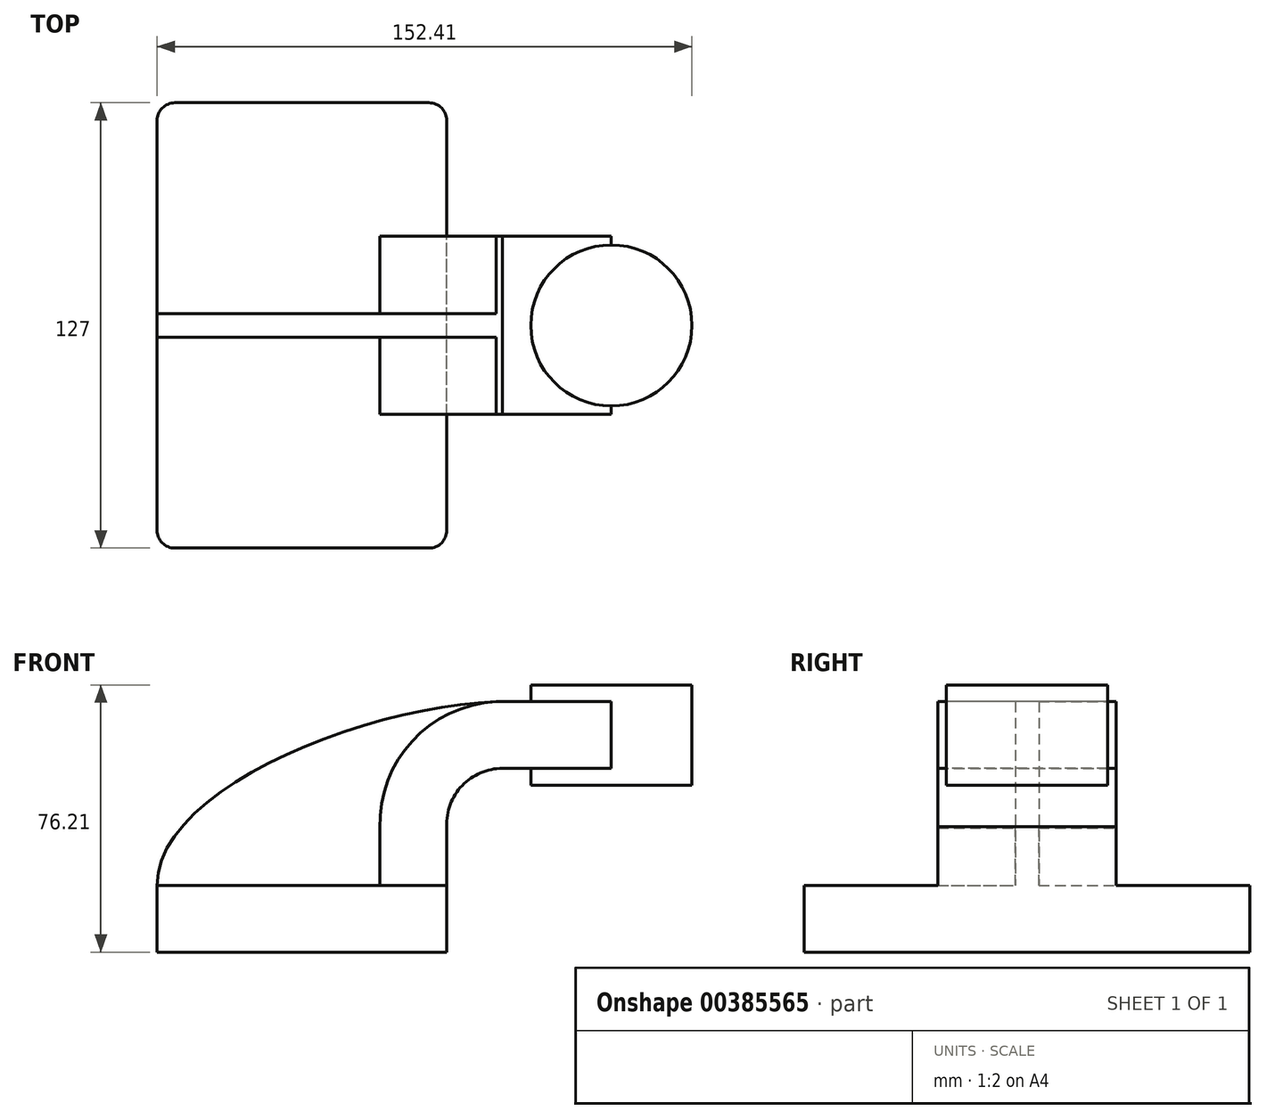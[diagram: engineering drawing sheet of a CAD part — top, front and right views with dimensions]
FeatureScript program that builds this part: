
annotation { "Feature Type Name" : "Feature", "Feature Type Description" : "" }
export const myFeature = defineFeature(function(context is Context, id is Id, definition is map)
    precondition{}
    {
        {
            var Q0;
            Q0=qCreatedBy(makeId("Front.planeOp"),FACE);
            var sketch = newSketch(context, id + "F0", { "sketchPlane" : qUnion([Q0])});
            skLineSegment(sketch, "E0.bottom", {"start": v(-41.28, 9.53) * mm, "end": v(41.27, 9.53) * mm});
            skLineSegment(sketch, "E0.top", {"start": v(-41.28, -9.52) * mm, "end": v(41.28, -9.52) * mm});
            skLineSegment(sketch, "E0.left", {"start": v(-41.28, 9.53) * mm, "end": v(-41.27, -9.52) * mm});
            skLineSegment(sketch, "E0.right", {"start": v(41.28, 9.53) * mm, "end": v(41.28, -9.52) * mm});
            skPoint(sketch, "E0.middle", {"position": v(0, 0) * mm});
            skLineSegment(sketch, "E1.bottom", {"start": v(60.33, 66.68) * mm, "end": v(111.12, 66.68) * mm});
            skLineSegment(sketch, "E1.top", {"start": v(60.33, 38.1) * mm, "end": v(111.12, 38.1) * mm});
            skLineSegment(sketch, "E1.left", {"start": v(60.33, 66.67) * mm, "end": v(60.33, 38.1) * mm});
            skLineSegment(sketch, "E1.right", {"start": v(111.12, 66.68) * mm, "end": v(111.12, 38.1) * mm});
            skLineSegment(sketch, "E2", {"start": v(41.27, 9.53) * mm, "end": v(41.27, 26.26) * mm});
            skArc(sketch, "E3", {"start": v(41.28, 26.26) * mm, "mid": v(45.65, 37.96) * mm, "end": v(57.13, 42.88) * mm});
            skLineSegment(sketch, "E4", {"start": v(57.13, 42.88) * mm, "end": v(88.16, 42.88) * mm});
            skLineSegment(sketch, "E5.0", {"start": v(57.13, 61.93) * mm, "end": v(88.16, 61.93) * mm});
            skArc(sketch, "E5.1", {"start": v(22.23, 25.9) * mm, "mid": v(32.05, 51.3) * mm, "end": v(57.13, 61.93) * mm});
            skLineSegment(sketch, "E5.2", {"start": v(22.22, 9.53) * mm, "end": v(22.22, 25.9) * mm});
            skLineSegment(sketch, "E6", {"start": v(88.16, 42.88) * mm, "end": v(88.16, 61.93) * mm});
            skLineSegment(sketch, "E7", {"start": v(88.16, 38.1) * mm, "end": v(88.16, 42.88) * mm});
            skLineSegment(sketch, "E8", {"start": v(88.16, 61.93) * mm, "end": v(88.16, 66.68) * mm});
            skFitSpline(sketch, "E9", {"points": [v(57.13, 61.93) * mm, v(-41.28, 9.53) * mm], "startDerivative": vector(-111, -1.8) * mm, "endDerivative": vector(0.4, -84.44) * mm});
            skSolve(sketch);
        }
        {
            var Q0;
            Q0=makeQuery(id+"F0.imprint","IMPRINT",FACE,{"disambiguationData":[TD([[makeQuery(id+"F0.imprint","IMPRINT",EDGE,{"derivedFrom":sQuery(id+"F0.wireOp",EDGE,"E0.top")}),1.0]])]});
            extrude(context, id + "F1", {"entities" : qUnion([Q0]), "endBound" : BoundingType.SYMMETRIC, "depth" : 127 * mm});
        }
        {
            var Q0;
            {var subQ6=sQuery(id+"F0.wireOp",EDGE,"E2");Q0=makeQuery(id+"F0.imprint","IMPRINT",FACE,{"disambiguationData":[TD([[makeQuery(id+"F0.imprint","IMPRINT",EDGE,{"derivedFrom":subQ6}),1.0]])]});}
            var Q1;
            {var subQ5=sQuery(id+"F0.wireOp",EDGE,"E6");Q1=makeQuery(id+"F0.imprint","IMPRINT",FACE,{"disambiguationData":[TD([[makeQuery(id+"F0.imprint","IMPRINT",EDGE,{"derivedFrom":subQ5}),1.0]])]});}
            extrude(context, id + "F2", {"entities" : qUnion([Q0, Q1]), "operationType" : NewBodyOperationType.ADD, "endBound" : BoundingType.SYMMETRIC, "depth" : 50.8 * mm});
        }
        {
            var Q0;
            {var subQ3=sQuery(id+"F0.wireOp",EDGE,"E5.2");Q0=makeQuery(id+"F0.imprint","IMPRINT",FACE,{"disambiguationData":[TD([[makeQuery(id+"F0.imprint","IMPRINT",EDGE,{"derivedFrom":subQ3}),1.0]])]});}
            extrude(context, id + "F3", {"entities" : qUnion([Q0]), "operationType" : NewBodyOperationType.ADD, "endBound" : BoundingType.SYMMETRIC, "depth" : 6.73 * mm});
        }
        {
            var Q0;
            Q0=makeQuery(id+"F1.opExtrude","CAP_EDGE",EDGE,{"disambiguationData":[OSD([sQuery(id+"F0.wireOp",EDGE,"E0.right")])],"isStart":false});
            var Q1;
            Q1=makeQuery(id+"F1.opExtrude","CAP_EDGE",EDGE,{"disambiguationData":[OSD([sQuery(id+"F0.wireOp",EDGE,"E0.left")])],"isStart":false});
            var Q2;
            Q2=makeQuery(id+"F1.opExtrude","CAP_EDGE",EDGE,{"disambiguationData":[OSD([sQuery(id+"F0.wireOp",EDGE,"E0.right")])],"isStart":true});
            var Q3;
            Q3=makeQuery(id+"F1.opExtrude","CAP_EDGE",EDGE,{"disambiguationData":[OSD([sQuery(id+"F0.wireOp",EDGE,"E0.left")])],"isStart":true});
            fillet(context, id + "F4", {"entities" : qUnion([Q0, Q1, Q2, Q3]), "radius" : 5.08 * mm, "tangentPropagation" : true, "allowEdgeOverflow" : false});
        }
        {
            var Q0;
            {var subQ0=sQuery(id+"F0.wireOp",EDGE,"E1.right");Q0=makeQuery(id+"F0.imprint","IMPRINT",FACE,{"disambiguationData":[TD([[makeQuery(id+"F0.imprint","IMPRINT",EDGE,{"derivedFrom":subQ0}),-1.0]])]});}
            var Q1;
            Q1=sQuery(id+"F0.wireOp",EDGE,"E6");
            revolve(context, id + "F5", {"operationType" : NewBodyOperationType.ADD, "entities" : qUnion([Q0]), "axis" : qUnion([Q1]), "revolveType" : RevolveType.FULL});
        }
    });
